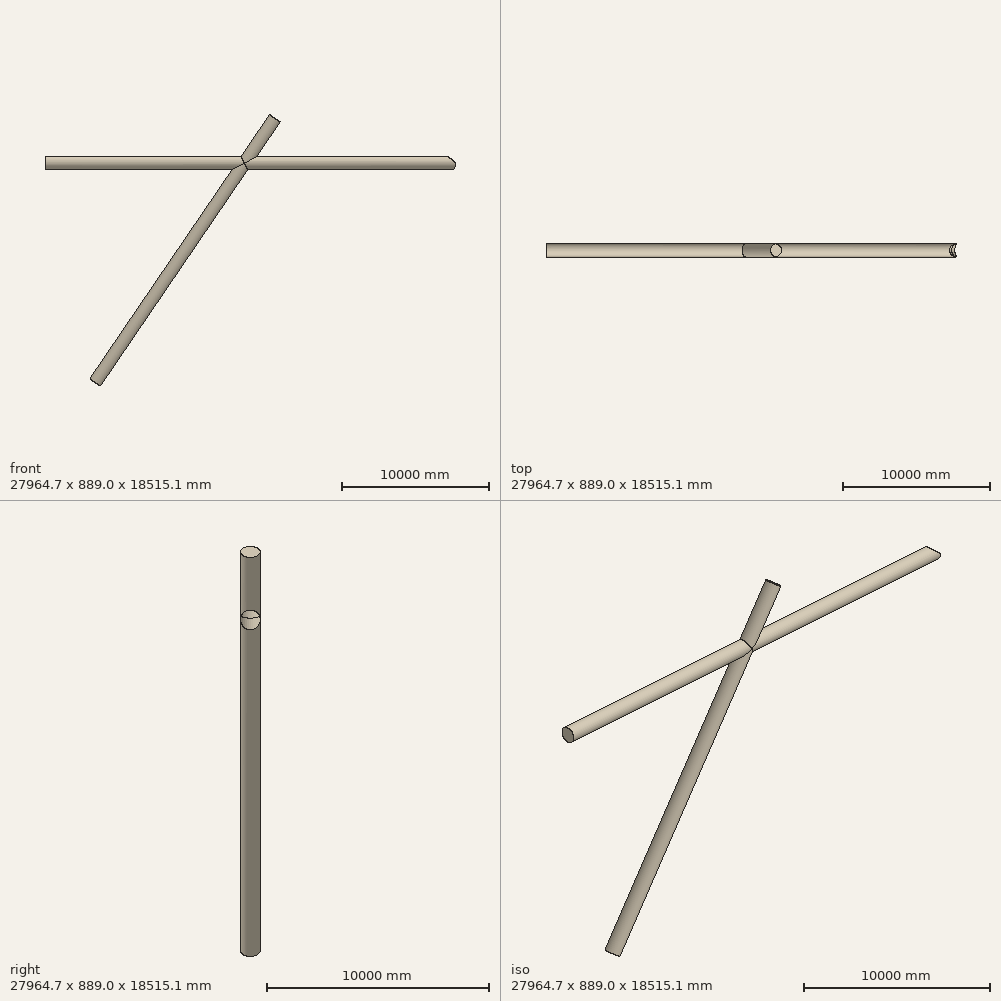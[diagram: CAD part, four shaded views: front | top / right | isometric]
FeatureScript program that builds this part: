
annotation { "Feature Type Name" : "Feature", "Feature Type Description" : "" }
export const myFeature = defineFeature(function(context is Context, id is Id, definition is map)
    precondition{}
    {
        {
            var Q0;
            Q0=qCreatedBy(makeId("Front.planeOp"),FACE);
            var sketch = newSketch(context, id + "F0", { "sketchPlane" : qUnion([Q0])});
            skCircle(sketch, "E0", {"center": v(0, 0) * mm, "radius": 508 * mm});
            skLineSegment(sketch, "E1", {"start": v(0, 0) * mm, "end": v(12084.62, 10097.6) * mm});
            skLineSegment(sketch, "E2", {"start": v(11708.9, 11041.57) * mm, "end": v(-3013.08, 10498.16) * mm});
            skLineSegment(sketch, "E3", {"start": v(-3013.07, 10498.16) * mm, "end": v(0, 0) * mm});
            skLineSegment(sketch, "E4", {"start": v(-10160, 0) * mm, "end": v(-3013.07, 10498.16) * mm});
            skLineSegment(sketch, "E5", {"start": v(0, 0) * mm, "end": v(-10160, 0) * mm});
            skLineSegment(sketch, "E6", {"start": v(12084.62, 10097.6) * mm, "end": v(12463.27, 9154.79) * mm});
            skLineSegment(sketch, "E7", {"start": v(12084.62, 10097.6) * mm, "end": v(11708.9, 11041.57) * mm});
            skLineSegment(sketch, "E8", {"start": v(11708.9, 11041.57) * mm, "end": v(11330.25, 11984.37) * mm});
            skLineSegment(sketch, "E9", {"start": v(-3013.08, 10498.16) * mm, "end": v(-3363.43, 11718.88) * mm});
            skLineSegment(sketch, "E10", {"start": v(0, 0) * mm, "end": v(-3363.43, 11718.88) * mm});
            skLineSegment(sketch, "E11.0", {"start": v(390.63, 112.11) * mm, "end": v(-2972.8, 11831) * mm});
            skLineSegment(sketch, "E12", {"start": v(-2972.8, 11831) * mm, "end": v(-3363.43, 11718.88) * mm});
            skLineSegment(sketch, "E13", {"start": v(390.63, 112.11) * mm, "end": v(0, 0) * mm});
            skLineSegment(sketch, "E14", {"start": v(12463.27, 9154.79) * mm, "end": v(11330.25, 11984.37) * mm});
            skLineSegment(sketch, "E15.0", {"start": v(12180.6, 11230.16) * mm, "end": v(11801.66, 12173.7) * mm});
            skLineSegment(sketch, "E15.1", {"start": v(12556.32, 10286.19) * mm, "end": v(12180.6, 11230.16) * mm});
            skLineSegment(sketch, "E15.2", {"start": v(12556.32, 10286.19) * mm, "end": v(12934.67, 9344.1) * mm});
            skLineSegment(sketch, "E16", {"start": v(11801.66, 12173.7) * mm, "end": v(11330.25, 11984.37) * mm});
            skLineSegment(sketch, "E17", {"start": v(12934.67, 9344.1) * mm, "end": v(12463.27, 9154.79) * mm});
            skSolve(sketch);
        }
        {
            var Q0;
            Q0=sQuery(id+"F0.wireOp",EDGE,"E11.0");
            var Q1;
            Q1=sQuery(id+"F0.wireOp",EDGE,"E12");
            var Q2;
            Q2=sQuery(id+"F0.wireOp",EDGE,"E13");
            var Q3;
            Q3=sQuery(id+"F0.wireOp",EDGE,"E10");
            revolve(context, id + "F1", {"bodyType" : ToolBodyType.SURFACE, "surfaceEntities" : qUnion([Q0, Q1, Q2]), "axis" : qUnion([Q3]), "revolveType" : RevolveType.FULL});
        }
        {
            var Q0;
            Q0=sQuery(id+"F0.wireOp",EDGE,"E15.1");
            var Q1;
            Q1=sQuery(id+"F0.wireOp",EDGE,"E15.0");
            var Q2;
            Q2=sQuery(id+"F0.wireOp",EDGE,"E15.2");
            var Q3;
            Q3=sQuery(id+"F0.wireOp",EDGE,"E17");
            var Q4;
            Q4=sQuery(id+"F0.wireOp",EDGE,"E16");
            var Q5;
            Q5=sQuery(id+"F0.wireOp",EDGE,"E6");
            revolve(context, id + "F2", {"bodyType" : ToolBodyType.SURFACE, "surfaceEntities" : qUnion([Q0, Q1, Q2, Q3, Q4]), "axis" : qUnion([Q5]), "revolveType" : RevolveType.FULL});
        }
        {
            var Q0;
            Q0=sQuery(id+"F0.wireOp",EDGE,"E2");
            cPoint(context, id + "F3", {"entities" : qUnion([Q0]), "parameter" : 0.5});
        }
        {
            var Q0;
            Q0=qCreatedBy(makeId("Right.planeOp"),FACE);
            var Q1;
            Q1 = qCreatedBy(id + "F3" ,VERTEX);
            cPlane(context, id + "F4", {"entities" : qUnion([Q0, Q1]), "cplaneType" : CPlaneType.PLANE_POINT, "offset" : 25.4 * mm, "width" : 152.4 * mm, "height" : 152.4 * mm});
        }
        {
            var Q0;
            Q0=qCreatedBy(id+"F4.planeOp",FACE);
            var sketch = newSketch(context, id + "F5", { "sketchPlane" : qUnion([Q0])});
            skCircle(sketch, "E18", {"center": v(0, 10769.87) * mm, "radius": 444.5 * mm});
            skSolve(sketch);
        }
        {
            var Q0;
            Q0 = qSketchRegion(id + "F5", true);
            extrude(context, id + "F6", {"entities" : qUnion([Q0]), "endBound" : BoundingType.UP_TO_NEXT, "depth" : 25.4 * mm, "hasSecondDirection" : true, "secondDirectionBound" : SecondDirectionBoundingType.THROUGH_ALL, "secondDirectionOppositeDirection" : true, "secondDirectionDepth" : 25.4 * mm});
        }
        {
            var Q0;
            Q0=sQuery(id+"F0.wireOp",EDGE,"E4");
            cPlane(context, id + "F7", {"entities" : qUnion([Q0]), "cplaneType" : CPlaneType.MID_PLANE, "offset" : 25.4 * mm, "width" : 152.4 * mm, "height" : 152.4 * mm});
        }
        {
            var Q0;
            Q0=qCreatedBy(id+"F7.planeOp",FACE);
            var sketch = newSketch(context, id + "F8", { "sketchPlane" : qUnion([Q0])});
            skCircle(sketch, "E19", {"center": v(-8398.53, 0) * mm, "radius": 444.5 * mm});
            skSolve(sketch);
        }
        {
            var Q0;
            Q0 = qSketchRegion(id + "F8", true);
            extrude(context, id + "F9", {"entities" : qUnion([Q0]), "operationType" : NewBodyOperationType.ADD, "depth" : 10388.6 * mm, "hasSecondDirection" : true, "secondDirectionOppositeDirection" : true, "secondDirectionDepth" : 11404.6 * mm});
        }
    });
